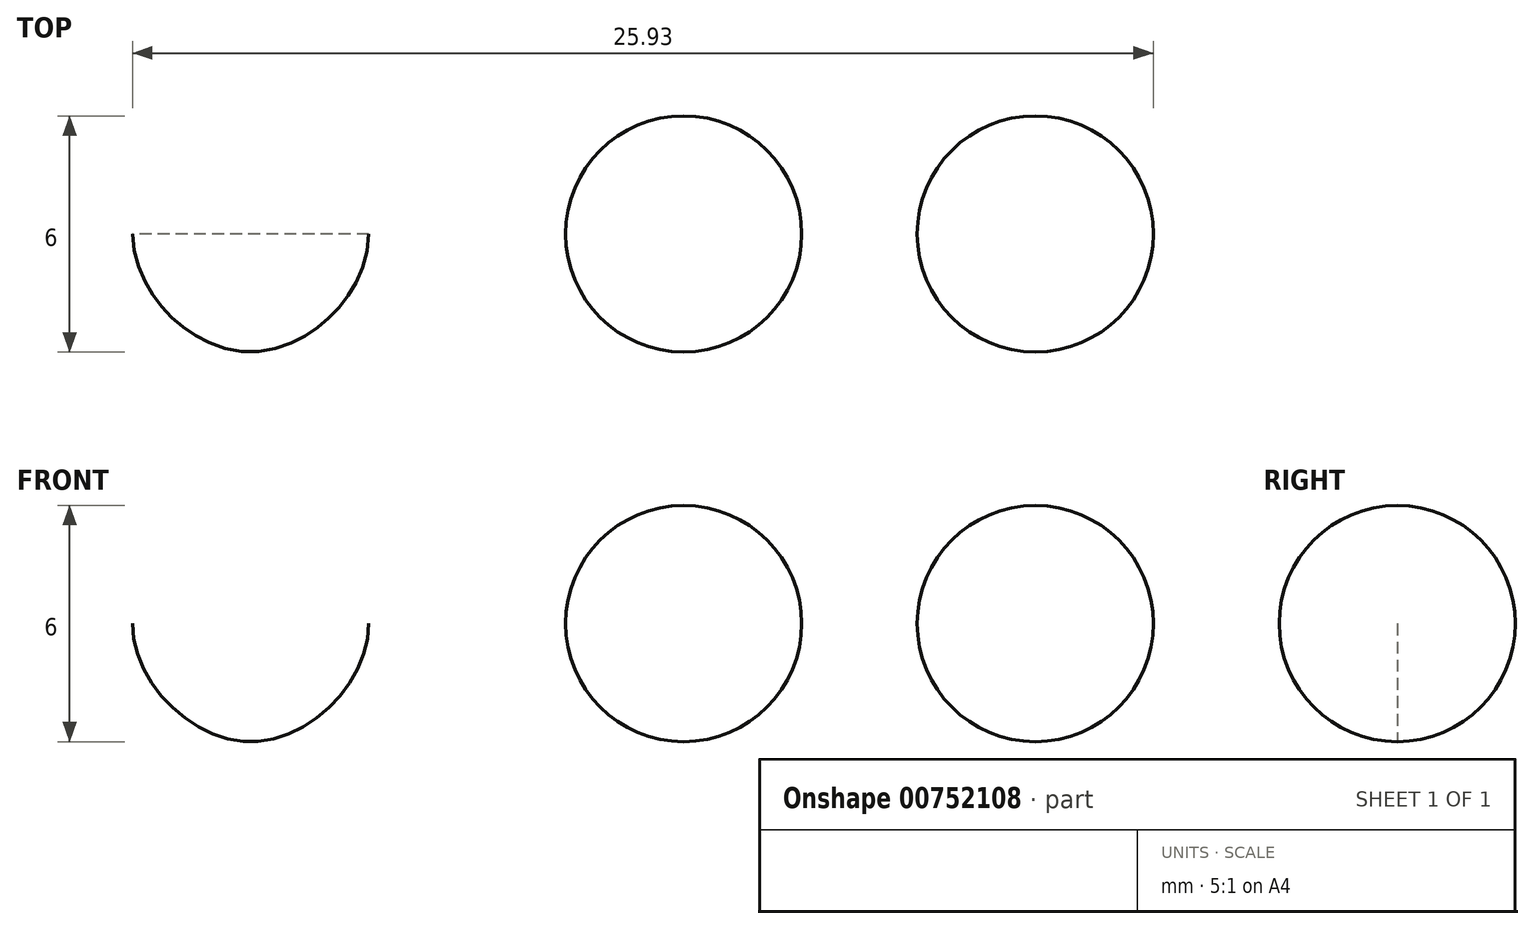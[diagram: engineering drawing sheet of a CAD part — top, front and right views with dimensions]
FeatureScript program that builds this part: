
annotation { "Feature Type Name" : "Feature", "Feature Type Description" : "" }
export const myFeature = defineFeature(function(context is Context, id is Id, definition is map)
    precondition{}
    {
        {
            var Q0;
            Q0=qCreatedBy(makeId("Front.planeOp"),FACE);
            var sketch = newSketch(context, id + "F0", { "sketchPlane" : qUnion([Q0])});
            skLineSegment(sketch, "E0", {"start": v(0, 3) * mm, "end": v(0, -3) * mm});
            skArc(sketch, "E1", {"start": v(0, -3) * mm, "mid": v(3, 0) * mm, "end": v(0, 3) * mm});
            skSolve(sketch);
        }
        {
            var Q0;
            Q0=makeQuery(id+"F0.imprint","IMPRINT",FACE,{"disambiguationData":[TD([[makeQuery(id+"F0.imprint","IMPRINT",EDGE,{"derivedFrom":sQuery(id+"F0.wireOp",EDGE,"E0")}),1.0]])]});
            var Q1;
            Q1=sQuery(id+"F0.wireOp",EDGE,"E0");
            revolve(context, id + "F1", {"surfaceOperationType" : NewSurfaceOperationType.NEW, "entities" : qUnion([Q0]), "axis" : qUnion([Q1]), "revolveType" : RevolveType.FULL});
        }
        {
            var Q0;
            Q0=qCreatedBy(makeId("Front.planeOp"),FACE);
            var sketch = newSketch(context, id + "F2", { "sketchPlane" : qUnion([Q0])});
            skCircle(sketch, "E2", {"center": v(8.93, 0) * mm, "radius": 3 * mm});
            skSolve(sketch);
        }
        {
            var Q0;
            Q0 = qSketchRegion(id + "F2", true);
            extrude(context, id + "F3", {"entities" : qUnion([Q0]), "endBound" : BoundingType.SYMMETRIC, "depth" : 6 * mm, "offsetDistance" : 25 * mm});
        }
        {
            var Q0;
            Q0=makeQuery(id+"F3.opExtrude","CAP_EDGE",EDGE,{"disambiguationData":[OSD([sQuery(id+"F2.wireOp",EDGE,"E2")])],"isStart":false});
            var Q1;
            Q1=makeQuery(id+"F3.opExtrude","CAP_EDGE",EDGE,{"disambiguationData":[OSD([sQuery(id+"F2.wireOp",EDGE,"E2")])],"isStart":true});
            fillet(context, id + "F4", {"entities" : qUnion([Q0, Q1]), "radius" : 3 * mm, "tangentPropagation" : true, "allowEdgeOverflow" : false});
        }
        {
            var Q0;
            Q0=qCreatedBy(makeId("Front.planeOp"),FACE);
            var sketch = newSketch(context, id + "F5", { "sketchPlane" : qUnion([Q0])});
            skLineSegment(sketch, "E3", {"start": v(-8, 0) * mm, "end": v(-11, 0) * mm});
            skLineSegment(sketch, "E4", {"start": v(-11, 0) * mm, "end": v(-14, 0) * mm});
            skSolve(sketch);
        }
        {
            var Q0;
            Q0=sQuery(id+"F5.wireOp",VERTEX,"E4.end");
            var Q1;
            Q1=sQuery(id+"F5.wireOp",EDGE,"E4");
            cPlane(context, id + "F6", {"entities" : qUnion([Q0, Q1]), "cplaneType" : CPlaneType.LINE_POINT, "offset" : 25 * mm, "width" : 150 * mm, "height" : 150 * mm});
        }
        {
            var Q0;
            Q0=sQuery(id+"F5.wireOp",VERTEX,"E3.start");
            var Q1;
            Q1=sQuery(id+"F5.wireOp",EDGE,"E3");
            cPlane(context, id + "F7", {"entities" : qUnion([Q0, Q1]), "cplaneType" : CPlaneType.LINE_POINT, "offset" : 25 * mm, "width" : 150 * mm, "height" : 150 * mm});
        }
        {
            var Q0;
            Q0=sQuery(id+"F5.wireOp",VERTEX,"E4.start");
            var Q1;
            Q1=sQuery(id+"F5.wireOp",EDGE,"E3");
            cPlane(context, id + "F8", {"entities" : qUnion([Q0, Q1]), "cplaneType" : CPlaneType.LINE_POINT, "offset" : 25 * mm, "width" : 150 * mm, "height" : 150 * mm});
        }
        {
            var Q0;
            Q0=qCreatedBy(id+"F7.planeOp",FACE);
            var sketch = newSketch(context, id + "F9", { "sketchPlane" : qUnion([Q0])});
            skPoint(sketch, "E5", {"position": v(0, 0) * mm});
            skSolve(sketch);
        }
        {
            var Q0;
            Q0=qCreatedBy(id+"F6.planeOp",FACE);
            var sketch = newSketch(context, id + "F10", { "sketchPlane" : qUnion([Q0])});
            skPoint(sketch, "E6", {"position": v(0, 0) * mm});
            skSolve(sketch);
        }
        {
            var Q0;
            Q0=qCreatedBy(id+"F8.planeOp",FACE);
            var sketch = newSketch(context, id + "F11", { "sketchPlane" : qUnion([Q0])});
            skCircle(sketch, "E7", {"center": v(0, 0) * mm, "radius": 3 * mm});
            skSolve(sketch);
        }
        {
            var Q0;
            Q0=sQuery(id+"F9.wireOp",VERTEX,"E5");
            var Q1;
            Q1=makeQuery(id+"F11.imprint","IMPRINT",FACE,{"disambiguationData":[TD([[makeQuery(id+"F11.imprint","IMPRINT",EDGE,{"derivedFrom":sQuery(id+"F11.wireOp",EDGE,"E7")}),1.0]])]});
            var Q2;
            Q2=sQuery(id+"F10.wireOp",VERTEX,"E6");
            loft(context, id + "F12", {"startCondition" : LoftEndDerivativeType.TANGENT_TO_PROFILE, "startMagnitude" : 1, "endCondition" : LoftEndDerivativeType.TANGENT_TO_PROFILE, "endMagnitude" : 1, "sheetProfilesArray" : [{ "sheetProfileEntities" : qUnion([Q0]) }, { "sheetProfileEntities" : qUnion([Q1]) }, { "sheetProfileEntities" : qUnion([Q2]) }]});
        }
    });
